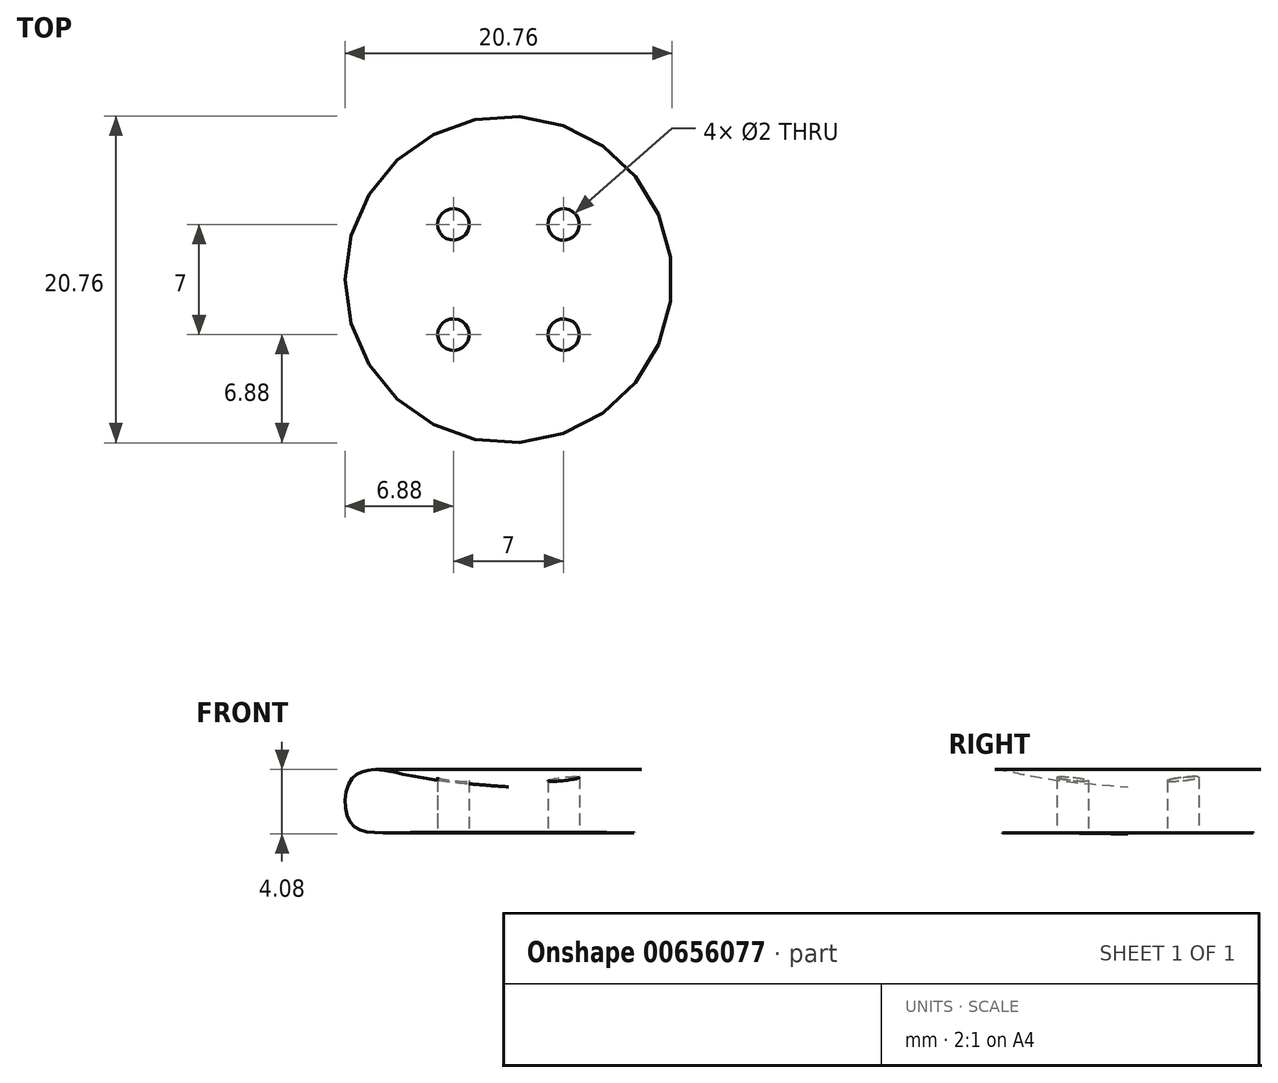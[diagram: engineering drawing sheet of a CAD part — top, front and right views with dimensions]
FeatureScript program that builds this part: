
annotation { "Feature Type Name" : "Feature", "Feature Type Description" : "" }
export const myFeature = defineFeature(function(context is Context, id is Id, definition is map)
    precondition{}
    {
        {
            var Q0;
            Q0=qCreatedBy(makeId("Front.planeOp"),FACE);
            var sketch = newSketch(context, id + "F0", { "sketchPlane" : qUnion([Q0])});
            skLineSegment(sketch, "E0.bottom", {"start": v(10, 0.08) * mm, "end": v(-10, 0.08) * mm, "construction": true});
            skLineSegment(sketch, "E0.top", {"start": v(10, 4.08) * mm, "end": v(-10, 4.08) * mm, "construction": true});
            skLineSegment(sketch, "E0.left", {"start": v(10, 0.08) * mm, "end": v(10, 4.08) * mm, "construction": true});
            skLineSegment(sketch, "E0.right", {"start": v(-10, 0.08) * mm, "end": v(-10, 4.08) * mm, "construction": true});
            skPoint(sketch, "E0.middle", {"position": v(0, 2.08) * mm});
            skFitSpline(sketch, "E1", {"points": [v(0, 0) * mm, v(-7.09, 0.08) * mm, v(-10, 0.67) * mm, v(-10, 3.44) * mm, v(-8.3, 4.08) * mm, v(0, 2.98) * mm], "startDerivative": vector(-30.04, 0.13) * mm, "endDerivative": vector(70.11, -4.67) * mm});
            skLineSegment(sketch, "E2", {"start": v(0, 2.98) * mm, "end": v(0, 0) * mm});
            skLineSegment(sketch, "E3", {"start": v(0, 0) * mm, "end": v(0, 7.86) * mm, "construction": true});
            skPoint(sketch, "E3.endSnap0", {"position": v(0, 4.08) * mm});
            skSolve(sketch);
        }
        {
            var Q0;
            Q0=makeQuery(id+"F0.imprint","IMPRINT",FACE,{"disambiguationData":[TD([[makeQuery(id+"F0.imprint","IMPRINT",EDGE,{"derivedFrom":sQuery(id+"F0.wireOp",EDGE,"E1")}),-1.0]])]});
            var Q1;
            Q1=sQuery(id+"F0.wireOp",EDGE,"E3");
            revolve(context, id + "F1", {"entities" : qUnion([Q0]), "axis" : qUnion([Q1]), "revolveType" : RevolveType.FULL});
        }
        {
            var Q0;
            Q0=qCreatedBy(makeId("Top.planeOp"),FACE);
            var sketch = newSketch(context, id + "F2", { "sketchPlane" : qUnion([Q0])});
            skLineSegment(sketch, "E4.bottom", {"start": v(3.5, -3.5) * mm, "end": v(-3.5, -3.5) * mm, "construction": true});
            skLineSegment(sketch, "E4.top", {"start": v(3.5, 3.5) * mm, "end": v(-3.5, 3.5) * mm, "construction": true});
            skLineSegment(sketch, "E4.left", {"start": v(3.5, -3.5) * mm, "end": v(3.5, 3.5) * mm, "construction": true});
            skLineSegment(sketch, "E4.right", {"start": v(-3.5, -3.5) * mm, "end": v(-3.5, 3.5) * mm, "construction": true});
            skPoint(sketch, "E4.middle", {"position": v(0, 0) * mm});
            skSolve(sketch);
        }
        {
            var Q0;
            Q0=sQuery(id+"F2.wireOp",VERTEX,"E4.right.start");
            var Q1;
            Q1=sQuery(id+"F2.wireOp",VERTEX,"E4.left.start");
            var Q2;
            Q2=sQuery(id+"F2.wireOp",VERTEX,"E4.top.end");
            var Q3;
            Q3=sQuery(id+"F2.wireOp",VERTEX,"E4.left.end");
            var Q4;
            Q4=makeQuery(id+"F1.opRevolve","SWEPT_BODY",BODY,{"disambiguationData":[OSD([sQuery(id+"F0.wireOp",EDGE,"E1"),sQuery(id+"F0.wireOp",EDGE,"E2")])]});
            hole(context, id + "F3", {"style" : HoleStyle.SIMPLE, "endStyle" : HoleEndStyle.BLIND, "oppositeDirection" : true, "holeDiameter" : 2 * mm, "majorDiameter" : 5 * mm, "holeDepth" : 6 * mm, "isTappedThrough" : true, "tappedDepth" : 12 * mm, "tapClearance" : 3, "startFromSketch" : true, "locations" : qUnion([Q0, Q1, Q2, Q3]), "scope" : qUnion([Q4])});
        }
    });
